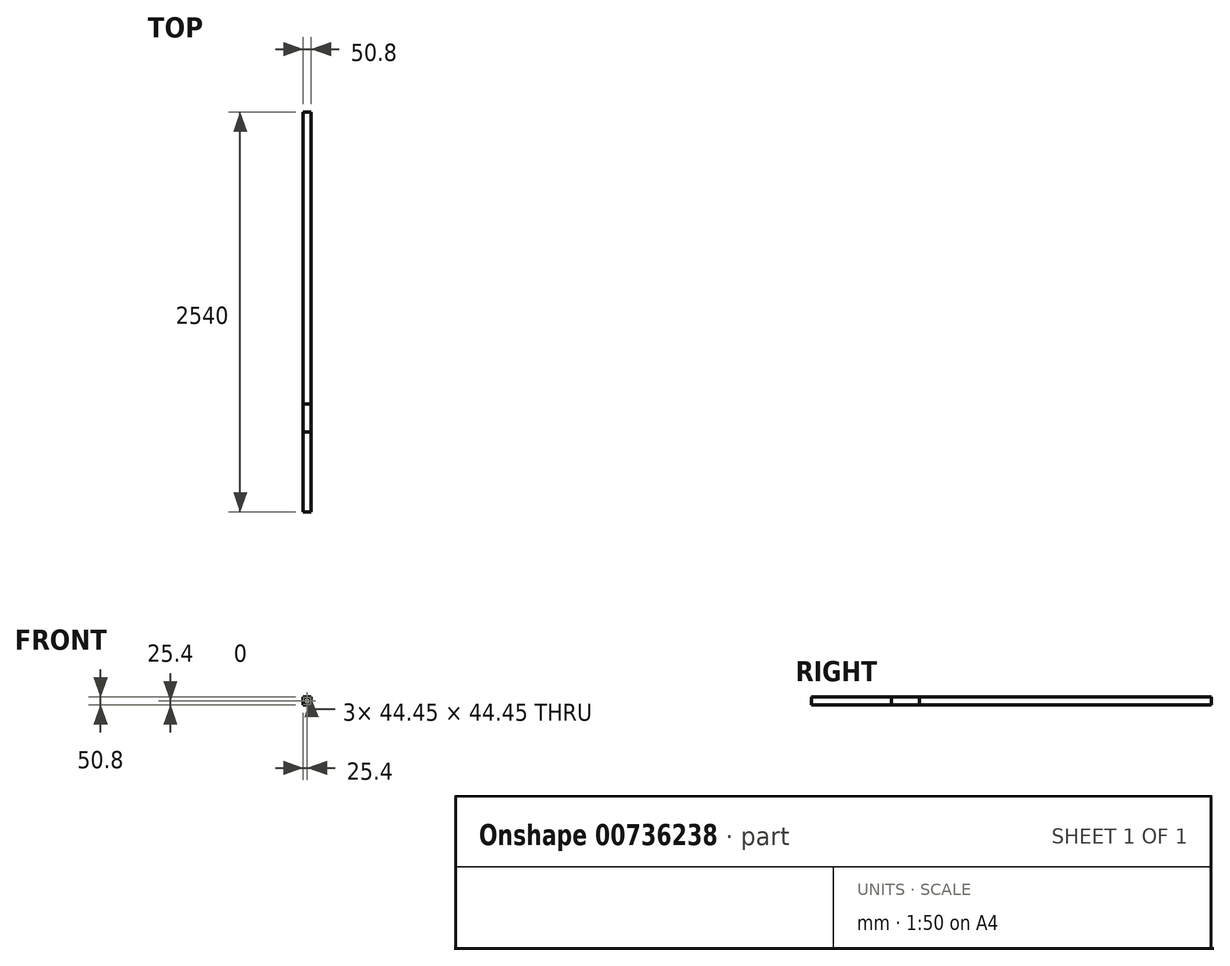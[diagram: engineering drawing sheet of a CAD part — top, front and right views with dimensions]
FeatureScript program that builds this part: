
annotation { "Feature Type Name" : "Feature", "Feature Type Description" : "" }
export const myFeature = defineFeature(function(context is Context, id is Id, definition is map)
    precondition{}
    {
        {
            var Q0;
            Q0=qCreatedBy(makeId("Front.planeOp"),FACE);
            var sketch = newSketch(context, id + "F0", { "sketchPlane" : qUnion([Q0])});
            skLineSegment(sketch, "E0.bottom", {"start": v(25.4, -25.4) * mm, "end": v(-25.4, -25.4) * mm});
            skLineSegment(sketch, "E0.top", {"start": v(25.4, 25.4) * mm, "end": v(-25.4, 25.4) * mm});
            skLineSegment(sketch, "E0.left", {"start": v(25.4, -25.4) * mm, "end": v(25.4, 25.4) * mm});
            skLineSegment(sketch, "E0.right", {"start": v(-25.4, -25.4) * mm, "end": v(-25.4, 25.4) * mm});
            skPoint(sketch, "E0.middle", {"position": v(0, 0) * mm});
            skLineSegment(sketch, "E1.bottom", {"start": v(22.23, -22.22) * mm, "end": v(-22.22, -22.23) * mm});
            skLineSegment(sketch, "E1.top", {"start": v(22.22, 22.23) * mm, "end": v(-22.23, 22.22) * mm});
            skLineSegment(sketch, "E1.left", {"start": v(22.23, -22.22) * mm, "end": v(22.22, 22.23) * mm});
            skLineSegment(sketch, "E1.right", {"start": v(-22.22, -22.23) * mm, "end": v(-22.23, 22.22) * mm});
            skSolve(sketch);
        }
        {
            var Q0;
            Q0 = qSketchRegion(id + "F0", true);
            extrude(context, id + "F1", {"entities" : qUnion([Q0]), "oppositeDirection" : true, "depth" : 2540 * mm, "offsetDistance" : 25.4 * mm});
        }
        {
            var Q0;
            Q0=makeQuery(id+"F0.imprint","IMPRINT",FACE,{"disambiguationData":[TD([[makeQuery(id+"F0.imprint","IMPRINT",EDGE,{"derivedFrom":sQuery(id+"F0.wireOp",EDGE,"E0.bottom")}),-1.0]])]});
            extrude(context, id + "F2", {"entities" : qUnion([Q0]), "oppositeDirection" : true, "depth" : 685.8 * mm, "offsetDistance" : 25.4 * mm});
        }
        {
            var Q0;
            Q0 = qSketchRegion(id + "F0", true);
            extrude(context, id + "F3", {"entities" : qUnion([Q0]), "oppositeDirection" : true, "depth" : 508 * mm, "offsetDistance" : 25.4 * mm});
        }
    });
